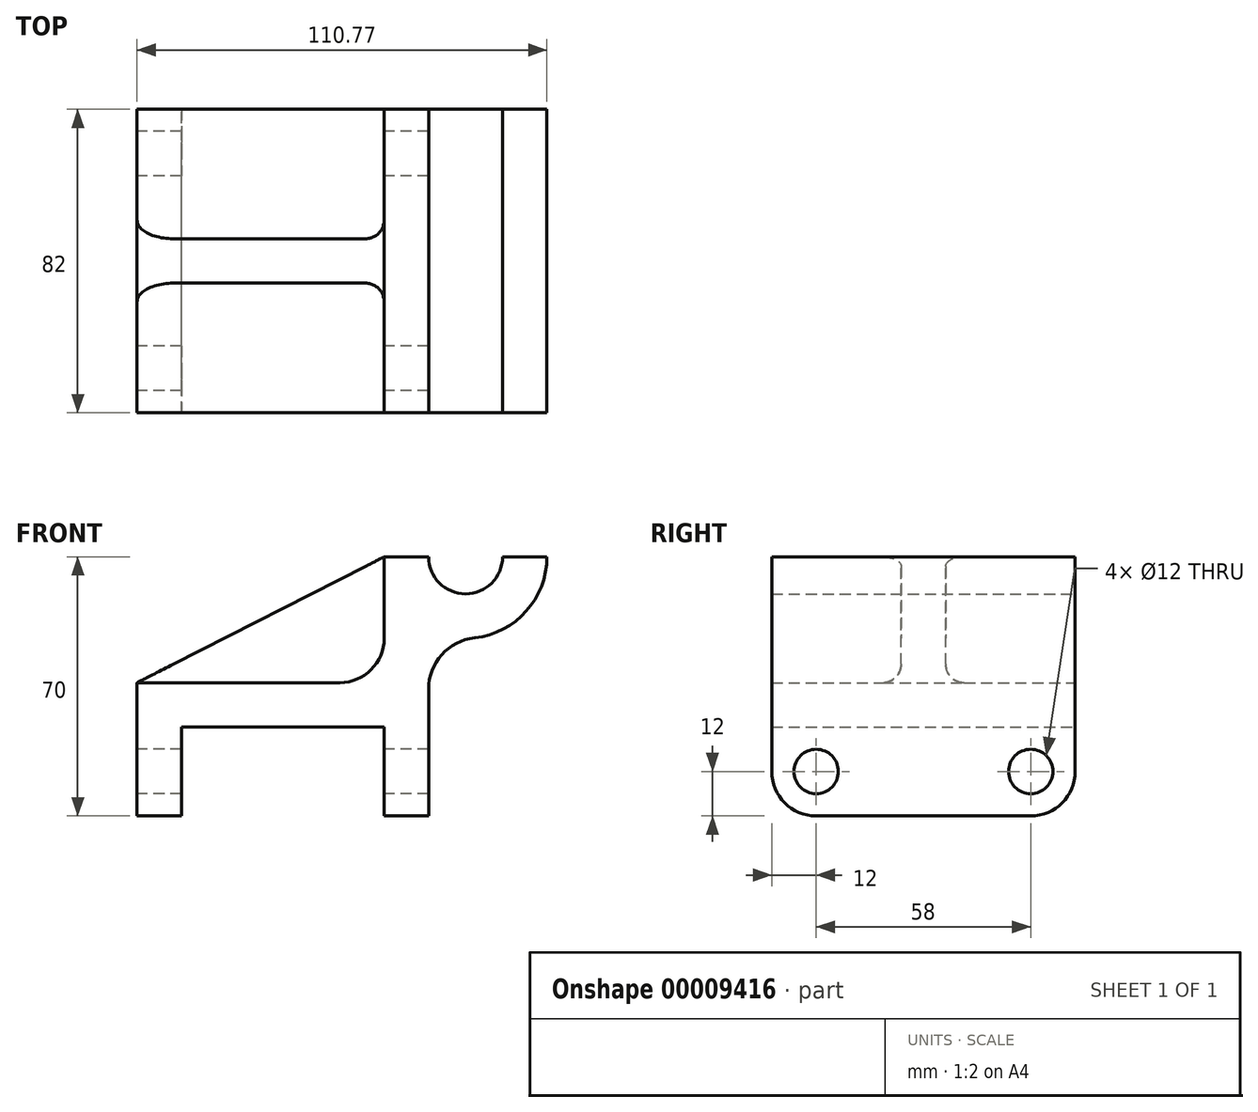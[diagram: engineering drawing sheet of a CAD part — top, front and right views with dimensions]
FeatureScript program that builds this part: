
annotation { "Feature Type Name" : "Feature", "Feature Type Description" : "" }
export const myFeature = defineFeature(function(context is Context, id is Id, definition is map)
    precondition{}
    {
        {
            var Q0;
            Q0=qCreatedBy(makeId("Front.planeOp"),FACE);
            var sketch = newSketch(context, id + "F0", { "sketchPlane" : qUnion([Q0])});
            skLineSegment(sketch, "E0", {"start": v(-23.07, 0) * mm, "end": v(-23.07, -36) * mm});
            skLineSegment(sketch, "E1", {"start": v(-23.07, -36) * mm, "end": v(-11.07, -36) * mm});
            skLineSegment(sketch, "E2", {"start": v(-11.07, -36) * mm, "end": v(-11.07, -12) * mm});
            skLineSegment(sketch, "E3", {"start": v(-11.07, -12) * mm, "end": v(43.7, -12) * mm});
            skLineSegment(sketch, "E4", {"start": v(43.7, -12) * mm, "end": v(43.7, -36) * mm});
            skLineSegment(sketch, "E5", {"start": v(43.7, -36) * mm, "end": v(55.7, -36) * mm});
            skLineSegment(sketch, "E6", {"start": v(55.7, -36) * mm, "end": v(55.7, -1.78) * mm});
            skLineSegment(sketch, "E7", {"start": v(55.7, 34) * mm, "end": v(43.7, 34) * mm});
            skLineSegment(sketch, "E8", {"start": v(43.7, 34) * mm, "end": v(43.7, 12) * mm});
            skLineSegment(sketch, "E9", {"start": v(31.7, 0) * mm, "end": v(-23.07, 0) * mm});
            skLineSegment(sketch, "E10", {"start": v(-23.07, 0) * mm, "end": v(43.7, 34) * mm});
            skLineSegment(sketch, "E11", {"start": v(55.7, 34) * mm, "end": v(101.4, 34) * mm, "construction": true});
            skArc(sketch, "E12", {"start": v(55.7, 34) * mm, "mid": v(65.7, 24) * mm, "end": v(75.7, 34) * mm});
            skArc(sketch, "E13", {"start": v(68.14, 12.14) * mm, "mid": v(82.1, 19.33) * mm, "end": v(87.7, 34) * mm});
            skLineSegment(sketch, "E14", {"start": v(75.7, 34) * mm, "end": v(87.7, 34) * mm});
            skArc(sketch, "E15", {"start": v(68.14, 12.14) * mm, "mid": v(59.26, 7.56) * mm, "end": v(55.7, -1.78) * mm});
            skPoint(sketch, "E16.orphan", {"position": v(43.7, 34) * mm});
            skPoint(sketch, "E17.visualSharp", {"position": v(43.7, 0) * mm});
            skArc(sketch, "E17.filletArc", {"start": v(31.7, 0) * mm, "mid": v(40.18, 3.51) * mm, "end": v(43.7, 12) * mm});
            skSolve(sketch);
        }
        {
            var Q0;
            Q0=makeQuery(id+"F0.imprint","IMPRINT",FACE,{"disambiguationData":[TD([[makeQuery(id+"F0.imprint","IMPRINT",EDGE,{"derivedFrom":sQuery(id+"F0.wireOp",EDGE,"E0")}),1.0]])]});
            extrude(context, id + "F1", {"entities" : qUnion([Q0]), "endBound" : BoundingType.SYMMETRIC, "depth" : 82 * mm});
        }
        {
            var Q0;
            Q0 = qSketchRegion(id + "F0", true);
            extrude(context, id + "F2", {"entities" : qUnion([Q0]), "operationType" : NewBodyOperationType.ADD, "endBound" : BoundingType.SYMMETRIC, "depth" : 12 * mm});
        }
        {
            var Q0;
            Q0=makeQuery(id+"F1.opExtrude","SWEPT_FACE",FACE,{"disambiguationData":[OSD([sQuery(id+"F0.wireOp",EDGE,"E0")])]});
            var sketch = newSketch(context, id + "F3", { "sketchPlane" : qUnion([Q0])});
            skCircle(sketch, "E18", {"center": v(-29, -24) * mm, "radius": 6 * mm});
            skLineSegment(sketch, "E19.bottom", {"start": v(-41, 0) * mm, "end": v(41, 0) * mm});
            skLineSegment(sketch, "E19.top", {"start": v(-29, -36) * mm, "end": v(29, -36) * mm});
            skLineSegment(sketch, "E19.left", {"start": v(-41, 0) * mm, "end": v(-41, -24) * mm});
            skLineSegment(sketch, "E19.right", {"start": v(41, 0) * mm, "end": v(41, -24) * mm});
            skPoint(sketch, "E20.visualSharp", {"position": v(-41, -36) * mm});
            skArc(sketch, "E20.filletArc", {"start": v(-41, -24) * mm, "mid": v(-37.49, -32.49) * mm, "end": v(-29, -36) * mm});
            skPoint(sketch, "E21.visualSharp", {"position": v(41, -36) * mm});
            skArc(sketch, "E21.filletArc", {"start": v(29, -36) * mm, "mid": v(37.49, -32.49) * mm, "end": v(41, -24) * mm});
            skCircle(sketch, "E22", {"center": v(29, -24) * mm, "radius": 6 * mm});
            skSolve(sketch);
        }
        {
            var Q0;
            Q0=makeQuery(id+"F3.imprint","IMPRINT",FACE,{"disambiguationData":[TD([[makeQuery(id+"F3.imprint","IMPRINT",EDGE,{"derivedFrom":sQuery(id+"F3.wireOp",EDGE,"E18")}),1.0]])]});
            var Q1;
            Q1=makeQuery(id+"F3.imprint","IMPRINT",FACE,{"disambiguationData":[TD([[makeQuery(id+"F3.imprint","IMPRINT",EDGE,{"derivedFrom":sQuery(id+"F3.wireOp",EDGE,"E22")}),1.0]])]});
            var Q2;
            {var subQ2=sQuery(id+"F3.wireOp",EDGE,"E21.filletArc");Q2=makeQuery(id+"F3.imprint","IMPRINT",FACE,{"disambiguationData":[TD([[makeQuery(id+"F3.imprint","IMPRINT",EDGE,{"derivedFrom":subQ2}),-1.0]])]});}
            var Q3;
            {var subQ2=sQuery(id+"F3.wireOp",EDGE,"E20.filletArc");Q3=makeQuery(id+"F3.imprint","IMPRINT",FACE,{"disambiguationData":[TD([[makeQuery(id+"F3.imprint","IMPRINT",EDGE,{"derivedFrom":subQ2}),-1.0]])]});}
            extrude(context, id + "F4", {"entities" : qUnion([Q0, Q1, Q2, Q3]), "operationType" : NewBodyOperationType.REMOVE, "endBound" : BoundingType.THROUGH_ALL, "oppositeDirection" : true, "depth" : 25 * mm});
        }
        {
            var Q0;
            Q0=makeQuery(id+"F2.boolean.opBoolean","INTERSECT",EDGE,{"derivedFrom":[makeQuery(id+"F1.opExtrude","SWEPT_FACE",FACE,{"disambiguationData":[OSD([sQuery(id+"F0.wireOp",EDGE,"E9")])]}),makeQuery(id+"F2.opExtrude","CAP_FACE",FACE,{"disambiguationData":[OSD([sQuery(id+"F0.wireOp",EDGE,"E0"),sQuery(id+"F0.wireOp",EDGE,"E1"),sQuery(id+"F0.wireOp",EDGE,"E2"),sQuery(id+"F0.wireOp",EDGE,"E3"),sQuery(id+"F0.wireOp",EDGE,"E4"),sQuery(id+"F0.wireOp",EDGE,"E5"),sQuery(id+"F0.wireOp",EDGE,"E6"),sQuery(id+"F0.wireOp",EDGE,"E7"),sQuery(id+"F0.wireOp",EDGE,"E10"),sQuery(id+"F0.wireOp",EDGE,"E12"),sQuery(id+"F0.wireOp",EDGE,"E13"),sQuery(id+"F0.wireOp",EDGE,"E14"),sQuery(id+"F0.wireOp",EDGE,"E15")])],"isStart":true})]});
            var Q1;
            Q1=makeQuery(id+"F2.boolean.opBoolean","INTERSECT",EDGE,{"derivedFrom":[makeQuery(id+"F1.opExtrude","SWEPT_FACE",FACE,{"disambiguationData":[OSD([sQuery(id+"F0.wireOp",EDGE,"E9")])]}),makeQuery(id+"F2.opExtrude","CAP_FACE",FACE,{"disambiguationData":[OSD([sQuery(id+"F0.wireOp",EDGE,"E0"),sQuery(id+"F0.wireOp",EDGE,"E1"),sQuery(id+"F0.wireOp",EDGE,"E2"),sQuery(id+"F0.wireOp",EDGE,"E3"),sQuery(id+"F0.wireOp",EDGE,"E4"),sQuery(id+"F0.wireOp",EDGE,"E5"),sQuery(id+"F0.wireOp",EDGE,"E6"),sQuery(id+"F0.wireOp",EDGE,"E7"),sQuery(id+"F0.wireOp",EDGE,"E10"),sQuery(id+"F0.wireOp",EDGE,"E12"),sQuery(id+"F0.wireOp",EDGE,"E13"),sQuery(id+"F0.wireOp",EDGE,"E14"),sQuery(id+"F0.wireOp",EDGE,"E15")])],"isStart":false})]});
            fillet(context, id + "F5", {"entities" : qUnion([Q0, Q1]), "radius" : 5 * mm, "tangentPropagation" : true, "allowEdgeOverflow" : false});
        }
    });
